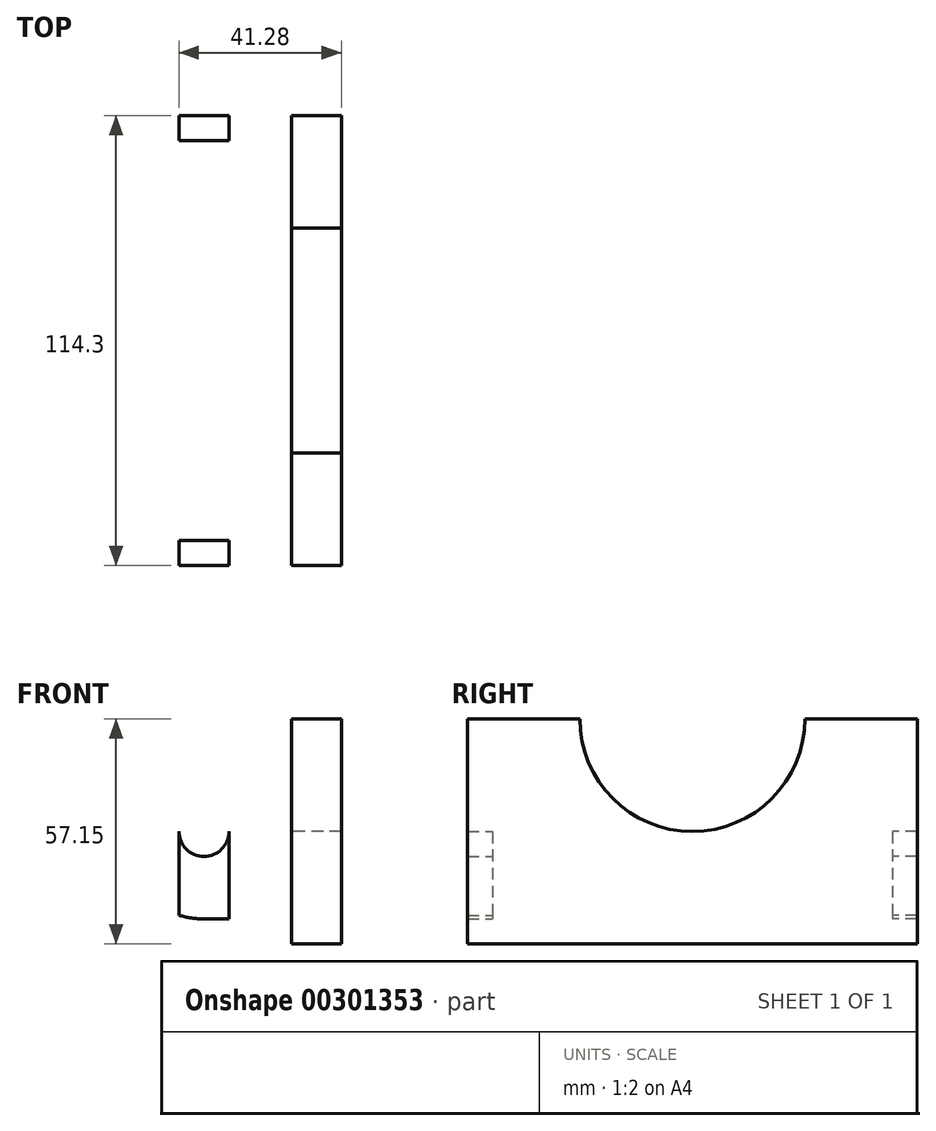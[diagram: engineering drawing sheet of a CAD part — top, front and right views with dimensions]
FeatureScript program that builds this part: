
annotation { "Feature Type Name" : "Feature", "Feature Type Description" : "" }
export const myFeature = defineFeature(function(context is Context, id is Id, definition is map)
    precondition{}
    {
        {
            var Q0;
            Q0=qCreatedBy(makeId("Front.planeOp"),FACE);
            var sketch = newSketch(context, id + "F0", { "sketchPlane" : qUnion([Q0])});
            skLineSegment(sketch, "E0.bottom", {"start": v(22.23, -22.22) * mm, "end": v(0, -22.23) * mm});
            skLineSegment(sketch, "E0.top", {"start": v(22.22, 22.23) * mm, "end": v(0, 22.23) * mm});
            skLineSegment(sketch, "E0.left", {"start": v(22.23, -22.23) * mm, "end": v(22.22, 22.23) * mm});
            skLineSegment(sketch, "E0.right", {"start": v(-22.23, 0) * mm, "end": v(-22.23, 0) * mm});
            skPoint(sketch, "E0.middle", {"position": v(0, 0) * mm});
            skPoint(sketch, "E1.visualSharp", {"position": v(-22.23, 22.22) * mm});
            skArc(sketch, "E1.filletArc", {"start": v(0, 22.23) * mm, "mid": v(-15.72, 15.72) * mm, "end": v(-22.23, 0) * mm});
            skCircle(sketch, "E2", {"center": v(0, 0) * mm, "radius": 6.35 * mm});
            skPoint(sketch, "E3.visualSharp", {"position": v(-22.22, -22.23) * mm});
            skArc(sketch, "E3.filletArc", {"start": v(-22.23, 0) * mm, "mid": v(-15.72, -15.72) * mm, "end": v(0, -22.23) * mm});
            skLineSegment(sketch, "E4.bottom", {"start": v(-6.35, 0) * mm, "end": v(6.35, 0) * mm});
            skLineSegment(sketch, "E4.top", {"start": v(-6.35, -22.23) * mm, "end": v(6.35, -22.23) * mm});
            skLineSegment(sketch, "E4.left", {"start": v(-6.35, 0) * mm, "end": v(-6.35, -22.23) * mm});
            skLineSegment(sketch, "E4.right", {"start": v(6.35, 0) * mm, "end": v(6.35, -22.23) * mm});
            skLineSegment(sketch, "E5.left", {"start": v(22.22, 22.23) * mm, "end": v(22.23, -34.92) * mm});
            skSolve(sketch);
        }
        {
            var Q0;
            Q0=qCreatedBy(makeId("Right.planeOp"),FACE);
            var sketch = newSketch(context, id + "F1", { "sketchPlane" : qUnion([Q0])});
            skLineSegment(sketch, "E6.bottom", {"start": v(57.15, -28.57) * mm, "end": v(-57.15, -28.58) * mm});
            skLineSegment(sketch, "E6.top", {"start": v(57.15, 28.58) * mm, "end": v(-57.15, 28.57) * mm});
            skLineSegment(sketch, "E6.left", {"start": v(57.15, -28.57) * mm, "end": v(57.15, 28.58) * mm});
            skLineSegment(sketch, "E6.right", {"start": v(-57.15, -28.58) * mm, "end": v(-57.15, 28.58) * mm});
            skPoint(sketch, "E6.middle", {"position": v(0, 0) * mm});
            skCircle(sketch, "E7", {"center": v(0, 28.58) * mm, "radius": 28.58 * mm});
            skSolve(sketch);
        }
        {
            var Q0;
            Q0=makeQuery(id+"F0.imprint","IMPRINT",FACE,{"disambiguationData":[TD([[makeQuery(id+"F0.imprint","IMPRINT",EDGE,{"derivedFrom":sQuery(id+"F0.wireOp",EDGE,"E0.bottom")}),-1.0]])]});
            var Q1;
            Q1=makeQuery(id+"F0.imprint","IMPRINT",FACE,{"disambiguationData":[TD([[makeQuery(id+"F0.imprint","IMPRINT",EDGE,{"derivedFrom":sQuery(id+"F0.wireOp",EDGE,"E5.bottom")}),1.0]])]});
            extrude(context, id + "F2", {"entities" : qUnion([Q0, Q1]), "depth" : 6.35 * mm});
        }
        {
            var Q0;
            Q0=makeQuery(id+"F2.opExtrude","SWEPT_BODY",BODY,{"disambiguationData":[OSD([sQuery(id+"F0.wireOp",EDGE,"E0.bottom"),sQuery(id+"F0.wireOp",EDGE,"E0.top"),sQuery(id+"F0.wireOp",EDGE,"E1.filletArc"),sQuery(id+"F0.wireOp",EDGE,"E2"),sQuery(id+"F0.wireOp",EDGE,"E3.filletArc"),sQuery(id+"F0.wireOp",EDGE,"E4.left"),sQuery(id+"F0.wireOp",EDGE,"E4.right"),sQuery(id+"F0.wireOp",EDGE,"E5.bottom"),sQuery(id+"F0.wireOp",EDGE,"E5.top"),sQuery(id+"F0.wireOp",EDGE,"E5.left")])]});
            var Q1;
            Q1=qCreatedBy(makeId("Front.planeOp"),FACE);
            transform(context, id + "F3", {"entities" : qUnion([Q0]), "transformType" : TransformType.TRANSLATION_3D, "dx" : -22.22 * mm, "dy" : -50.8 * mm, "dz" : 0 * mm, "makeCopy" : false});
        }
        {
            var Q0;
            Q0=makeQuery(id+"F2.opExtrude","SWEPT_BODY",BODY,{"disambiguationData":[OSD([sQuery(id+"F0.wireOp",EDGE,"E0.bottom"),sQuery(id+"F0.wireOp",EDGE,"E0.top"),sQuery(id+"F0.wireOp",EDGE,"E1.filletArc"),sQuery(id+"F0.wireOp",EDGE,"E2"),sQuery(id+"F0.wireOp",EDGE,"E3.filletArc"),sQuery(id+"F0.wireOp",EDGE,"E4.left"),sQuery(id+"F0.wireOp",EDGE,"E4.right"),sQuery(id+"F0.wireOp",EDGE,"E5.bottom"),sQuery(id+"F0.wireOp",EDGE,"E5.top"),sQuery(id+"F0.wireOp",EDGE,"E5.left")])]});
            var Q1;
            Q1=qCreatedBy(makeId("Front.planeOp"),FACE);
            mirror(context, id + "F4", {"entities" : qUnion([Q0]), "mirrorPlane" : qUnion([Q1])});
        }
        {
            var Q0;
            Q0=makeQuery(id+"F1.imprint","IMPRINT",FACE,{"disambiguationData":[TD([[makeQuery(id+"F1.imprint","IMPRINT",EDGE,{"derivedFrom":sQuery(id+"F1.wireOp",EDGE,"E6.bottom")}),-1.0]])]});
            extrude(context, id + "F5", {"entities" : qUnion([Q0]), "depth" : 12.7 * mm});
        }
    });
